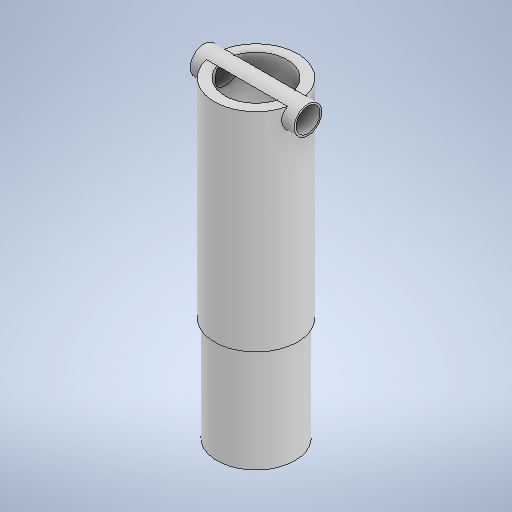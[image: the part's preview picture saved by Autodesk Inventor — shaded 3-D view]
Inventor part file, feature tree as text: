
AUTODESK INVENTOR PART (.ipt)
format: ipt  version: 2025 (Build 290162000, 162)  size: 285,696 bytes
history: native  units: in
note: dims shown in document units (in); Inventor stores cm internally (conversion verified against a paired STEP export)
features: sketch x5, extrude x4, hole x1
ambient origin geometry x8: Origin, YZ Plane, XZ Plane, XY Plane, X Axis, Y Axis, Z Axis, Center Point
bodies: Solid1 (feature_tree)
feature tree (10):
  extrude  "Extrusion1"  Depth=11.811in TaperAngle=0.0deg
  extrude  "Extrusion2"  Depth=1.0433in
  extrude  "Extrusion4"  Depth=3.1496in
  extrude  "Extrusion5"  Depth=2.3622in
  hole  "Hole1"  [1 undecoded]
  sketch  "Sketch1"  dims[d0=2.9528in d1=11.811in d2=0.0in]
  sketch  "Sketch2"  dims[d3=11.4173in d4=1.0433in]
  sketch  "Sketch4"  dims[d5=3.937in d6=0.0in d9=3.1496in]
  sketch  "Sketch5"  dims[d10=7.874in d11=0.0in d12=2.3622in]
  sketch  "Sketch6"  dims[d13=9.8425in d14=0.0in d15=0.9055in d16=2.0in d17=0.1575in d18=0.0787in d19=90.0deg d20=0.315in d21=0.8108in]
note: 1 required parameter value undecoded (feature->parameter linkage not recoverable at this tier; creation-order binding heuristic only, values carry confidence <= 0.55)
